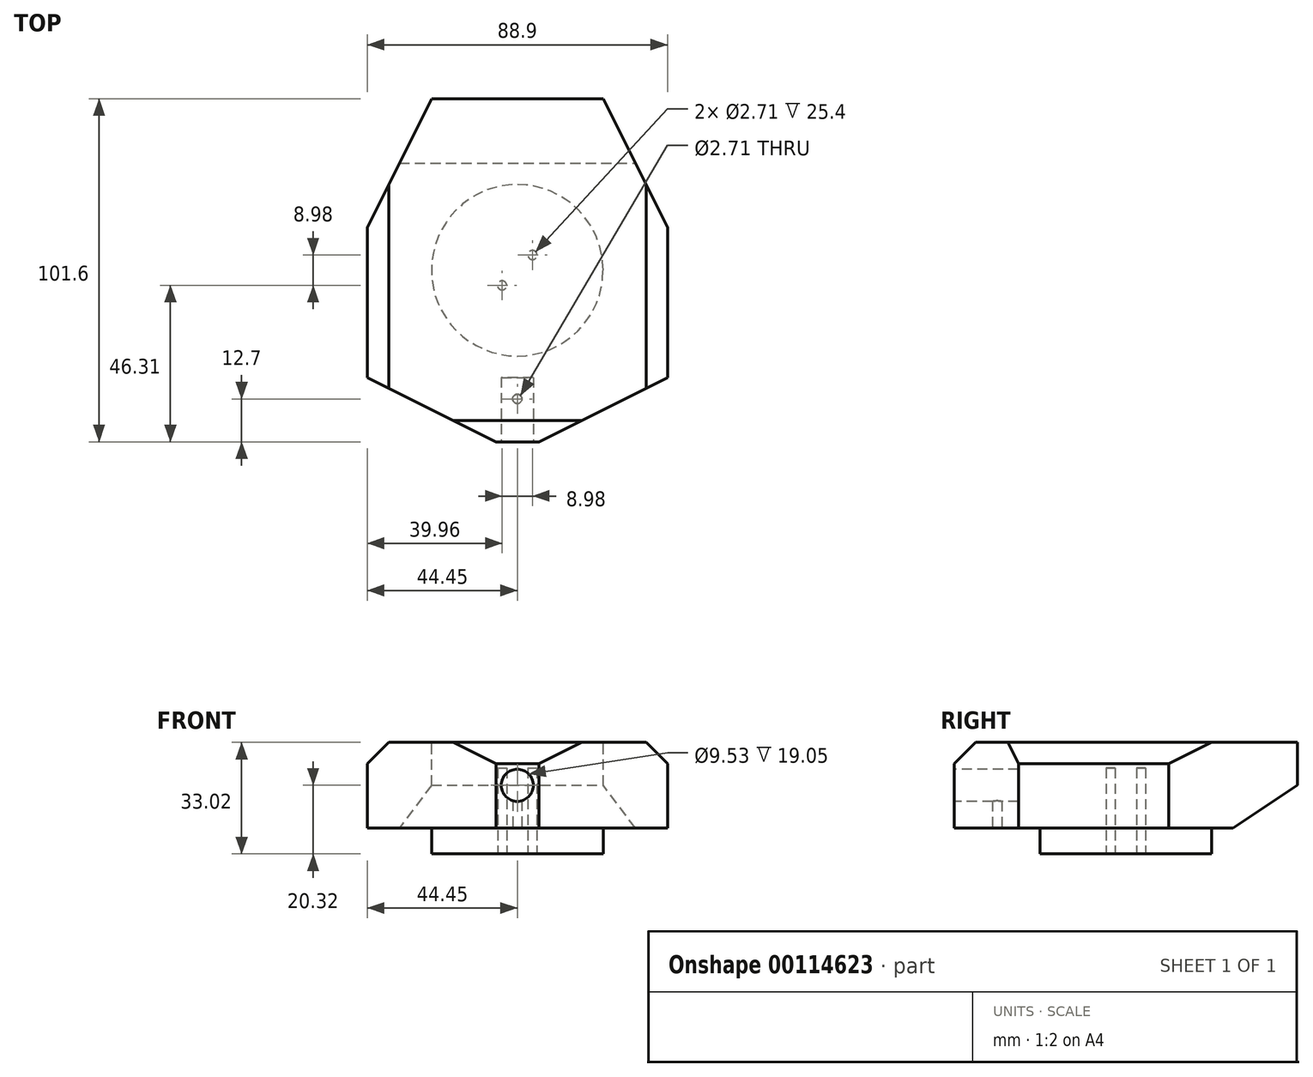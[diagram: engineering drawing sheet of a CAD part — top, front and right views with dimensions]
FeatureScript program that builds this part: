
annotation { "Feature Type Name" : "Feature", "Feature Type Description" : "" }
export const myFeature = defineFeature(function(context is Context, id is Id, definition is map)
    precondition{}
    {
        {
            var Q0;
            Q0=qCreatedBy(makeId("Front.planeOp"),FACE);
            var sketch = newSketch(context, id + "F0", { "sketchPlane" : qUnion([Q0])});
            skLineSegment(sketch, "E0.bottom", {"start": v(44.45, -12.7) * mm, "end": v(-44.45, -12.7) * mm});
            skLineSegment(sketch, "E0.top", {"start": v(44.45, 12.7) * mm, "end": v(-44.45, 12.7) * mm});
            skLineSegment(sketch, "E0.left", {"start": v(44.45, -12.7) * mm, "end": v(44.45, 12.7) * mm});
            skLineSegment(sketch, "E0.right", {"start": v(-44.45, -12.7) * mm, "end": v(-44.45, 12.7) * mm});
            skPoint(sketch, "E0.middle", {"position": v(0, 0) * mm});
            skSolve(sketch);
        }
        {
            var Q0;
            Q0 = qSketchRegion(id + "F0", true);
            extrude(context, id + "F1", {"entities" : qUnion([Q0]), "endBound" : BoundingType.SYMMETRIC, "depth" : 101.6 * mm});
        }
        {
            var Q0;
            Q0=makeQuery(id+"F1.opExtrude","SWEPT_FACE",FACE,{"disambiguationData":[OSD([sQuery(id+"F0.wireOp",EDGE,"E0.top")])]});
            var sketch = newSketch(context, id + "F2", { "sketchPlane" : qUnion([Q0])});
            skPoint(sketch, "E1", {"position": v(0, -50.8) * mm});
            skPoint(sketch, "E2", {"position": v(6.35, -50.8) * mm});
            skPoint(sketch, "E3", {"position": v(-6.35, -50.8) * mm});
            skPoint(sketch, "E4", {"position": v(-44.45, -50.8) * mm});
            skPoint(sketch, "E5", {"position": v(44.45, -50.8) * mm});
            skPoint(sketch, "E6", {"position": v(44.45, -31.75) * mm});
            skPoint(sketch, "E7", {"position": v(-44.45, -31.75) * mm});
            skLineSegment(sketch, "E8", {"start": v(-44.45, -31.75) * mm, "end": v(-6.35, -50.8) * mm});
            skLineSegment(sketch, "E9", {"start": v(-6.35, -50.8) * mm, "end": v(6.35, -50.8) * mm});
            skLineSegment(sketch, "E10", {"start": v(6.35, -50.8) * mm, "end": v(44.45, -31.75) * mm});
            skLineSegment(sketch, "E11", {"start": v(44.45, -31.75) * mm, "end": v(44.45, -50.8) * mm});
            skLineSegment(sketch, "E12", {"start": v(44.45, -50.8) * mm, "end": v(6.35, -50.8) * mm});
            skLineSegment(sketch, "E13", {"start": v(-6.35, -50.8) * mm, "end": v(-44.45, -50.8) * mm});
            skLineSegment(sketch, "E14", {"start": v(-44.45, -50.8) * mm, "end": v(-44.45, -31.75) * mm});
            skLineSegment(sketch, "E15", {"start": v(-44.45, 50.8) * mm, "end": v(-44.45, 12.7) * mm});
            skLineSegment(sketch, "E16", {"start": v(44.45, 50.8) * mm, "end": v(44.45, 12.7) * mm});
            skLineSegment(sketch, "E17", {"start": v(-44.45, 50.8) * mm, "end": v(-25.4, 50.8) * mm});
            skLineSegment(sketch, "E18", {"start": v(44.45, 50.8) * mm, "end": v(25.4, 50.8) * mm});
            skLineSegment(sketch, "E19", {"start": v(25.4, 50.8) * mm, "end": v(44.45, 12.7) * mm});
            skLineSegment(sketch, "E20", {"start": v(-25.4, 50.8) * mm, "end": v(-44.45, 12.7) * mm});
            skSolve(sketch);
        }
        {
            var Q0;
            Q0 = qSketchRegion(id + "F2", true);
            extrude(context, id + "F3", {"entities" : qUnion([Q0]), "operationType" : NewBodyOperationType.REMOVE, "oppositeDirection" : true, "depth" : 25.4 * mm});
        }
        {
            var Q0;
            Q0=qCreatedBy(makeId("Right.planeOp"),FACE);
            var sketch = newSketch(context, id + "F4", { "sketchPlane" : qUnion([Q0])});
            skLineSegment(sketch, "E21.0", {"start": v(50.8, -12.7) * mm, "end": v(50.8, 12.7) * mm, "construction": true});
            skPoint(sketch, "E22", {"position": v(50.8, 0) * mm});
            skLineSegment(sketch, "E23", {"start": v(50.8, 0) * mm, "end": v(50.8, -12.7) * mm, "construction": true});
            skLineSegment(sketch, "E24", {"start": v(50.8, -12.7) * mm, "end": v(31.75, -12.7) * mm, "construction": true});
            skLineSegment(sketch, "E25", {"start": v(31.75, -12.7) * mm, "end": v(50.8, 0) * mm});
            skLineSegment(sketch, "E26", {"start": v(31.75, -12.7) * mm, "end": v(50.8, -12.7) * mm});
            skLineSegment(sketch, "E27", {"start": v(50.8, 0) * mm, "end": v(50.8, -12.7) * mm});
            skSolve(sketch);
        }
        {
            var Q0;
            Q0 = qSketchRegion(id + "F4", true);
            extrude(context, id + "F5", {"entities" : qUnion([Q0]), "operationType" : NewBodyOperationType.REMOVE, "endBound" : BoundingType.THROUGH_ALL, "oppositeDirection" : true, "depth" : 25.4 * mm});
        }
        {
            var Q0;
            Q0=makeQuery(id+"F5.boolean.opBoolean","COPY",FACE,{"derivedFrom":makeQuery(id+"F5.opExtrude","CAP_FACE",FACE,{"disambiguationData":[OSD([sQuery(id+"F4.wireOp",EDGE,"E25"),sQuery(id+"F4.wireOp",EDGE,"E26"),sQuery(id+"F4.wireOp",EDGE,"E27")])],"isStart":true})});
            extrude(context, id + "F6", {"entities" : qUnion([Q0]), "operationType" : NewBodyOperationType.REMOVE, "endBound" : BoundingType.THROUGH_ALL, "oppositeDirection" : true, "depth" : 25.4 * mm});
        }
        {
            var Q0;
            Q0=makeQuery(id+"F3.boolean.opBoolean","COPY",EDGE,{"derivedFrom":makeQuery(id+"F3.opExtrude","CAP_EDGE",EDGE,{"disambiguationData":[OSD([sQuery(id+"F2.wireOp",EDGE,"E10")])],"isStart":true})});
            var Q1;
            Q1=makeQuery(id+"F1.opExtrude","CAP_EDGE",EDGE,{"disambiguationData":[OSD([sQuery(id+"F0.wireOp",EDGE,"E0.top")])],"isStart":false});
            var Q2;
            Q2=makeQuery(id+"F3.boolean.opBoolean","COPY",EDGE,{"derivedFrom":makeQuery(id+"F3.opExtrude","CAP_EDGE",EDGE,{"disambiguationData":[OSD([sQuery(id+"F2.wireOp",EDGE,"E8")])],"isStart":true})});
            var Q3;
            Q3=makeQuery(id+"F1.opExtrude","SWEPT_EDGE",EDGE,{"disambiguationData":[OSD([sQuery(id+"F0.wireOp",EDGE,"E0.top"),sQuery(id+"F0.wireOp",EDGE,"E0.right")])]});
            var Q4;
            Q4=makeQuery(id+"F3.boolean.opBoolean","COPY",EDGE,{"derivedFrom":makeQuery(id+"F3.opExtrude","CAP_EDGE",EDGE,{"disambiguationData":[OSD([sQuery(id+"F2.wireOp",EDGE,"E20")])],"isStart":true})});
            var Q5;
            Q5=makeQuery(id+"F1.opExtrude","SWEPT_EDGE",EDGE,{"disambiguationData":[OSD([sQuery(id+"F0.wireOp",EDGE,"E0.top"),sQuery(id+"F0.wireOp",EDGE,"E0.left")])]});
            var Q6;
            Q6=makeQuery(id+"F3.boolean.opBoolean","COPY",EDGE,{"derivedFrom":makeQuery(id+"F3.opExtrude","CAP_EDGE",EDGE,{"disambiguationData":[OSD([sQuery(id+"F2.wireOp",EDGE,"E19")])],"isStart":true})});
            chamfer(context, id + "F7", {"entities" : qUnion([Q0, Q1, Q2, Q3, Q4, Q5, Q6]), "width" : 6.35 * mm, "tangentPropagation" : true});
        }
        {
            var Q0;
            Q0=makeQuery(id+"F1.opExtrude","SWEPT_FACE",FACE,{"disambiguationData":[OSD([sQuery(id+"F0.wireOp",EDGE,"E0.bottom")])]});
            var sketch = newSketch(context, id + "F8", { "sketchPlane" : qUnion([Q0])});
            skCircle(sketch, "E28", {"center": v(0, 0) * mm, "radius": 25.4 * mm});
            skLineSegment(sketch, "E29", {"start": v(0, 0) * mm, "end": v(20.32, 0) * mm, "construction": true});
            skSolve(sketch);
        }
        {
            var Q0;
            Q0 = qSketchRegion(id + "F8", true);
            extrude(context, id + "F9", {"entities" : qUnion([Q0]), "operationType" : NewBodyOperationType.ADD, "depth" : 7.62 * mm});
        }
        {
            var Q0;
            Q0=makeQuery(id+"F9.opExtrude","CAP_FACE",FACE,{"disambiguationData":[OSD([sQuery(id+"F8.wireOp",EDGE,"E28")])],"isStart":false});
            var sketch = newSketch(context, id + "F10", { "sketchPlane" : qUnion([Q0])});
            skLineSegment(sketch, "E30", {"start": v(0, 0) * mm, "end": v(6.09, 0) * mm});
            skLineSegment(sketch, "E31", {"start": v(0, 0) * mm, "end": v(4.58, 4.58) * mm, "construction": true});
            skLineSegment(sketch, "E32", {"start": v(0, 0) * mm, "end": v(4.5, -4.5) * mm, "construction": true});
            skCircle(sketch, "E33", {"center": v(4.5, -4.5) * mm, "radius": 1.35 * mm});
            skCircle(sketch, "E34.MirrorC", {"center": v(-4.5, 4.5) * mm, "radius": 1.35 * mm});
            skSolve(sketch);
        }
        {
            var Q0;
            Q0 = qSketchRegion(id + "F10", true);
            extrude(context, id + "F11", {"entities" : qUnion([Q0]), "operationType" : NewBodyOperationType.REMOVE, "oppositeDirection" : true, "depth" : 25.4 * mm});
        }
        {
            var Q0;
            Q0=makeQuery(id+"F1.opExtrude","CAP_FACE",FACE,{"disambiguationData":[OSD([sQuery(id+"F0.wireOp",EDGE,"E0.bottom"),sQuery(id+"F0.wireOp",EDGE,"E0.top"),sQuery(id+"F0.wireOp",EDGE,"E0.left"),sQuery(id+"F0.wireOp",EDGE,"E0.right")])],"isStart":false});
            var sketch = newSketch(context, id + "F12", { "sketchPlane" : qUnion([Q0])});
            skCircle(sketch, "E35", {"center": v(0, 0) * mm, "radius": 4.76 * mm});
            skSolve(sketch);
        }
        {
            var Q0;
            Q0=makeQuery(id+"F12.imprint","IMPRINT",FACE,{"disambiguationData":[TD([[makeQuery(id+"F12.imprint","IMPRINT",EDGE,{"derivedFrom":sQuery(id+"F12.wireOp",EDGE,"E35")}),1.0]])]});
            extrude(context, id + "F13", {"entities" : qUnion([Q0]), "operationType" : NewBodyOperationType.REMOVE, "oppositeDirection" : true, "depth" : 19.05 * mm});
        }
        {
            var Q0;
            Q0=makeQuery(id+"F1.opExtrude","SWEPT_FACE",FACE,{"disambiguationData":[OSD([sQuery(id+"F0.wireOp",EDGE,"E0.bottom")])]});
            var sketch = newSketch(context, id + "F14", { "sketchPlane" : qUnion([Q0])});
            skLineSegment(sketch, "E36", {"start": v(0, 50.8) * mm, "end": v(0, 38.1) * mm, "construction": true});
            skPoint(sketch, "E36.endSnap0", {"position": v(0, 50.8) * mm});
            skCircle(sketch, "E37", {"center": v(0, 38.1) * mm, "radius": 1.35 * mm});
            skSolve(sketch);
        }
        {
            var Q0;
            Q0=makeQuery(id+"F14.imprint","IMPRINT",FACE,{"disambiguationData":[TD([[makeQuery(id+"F14.imprint","IMPRINT",EDGE,{"derivedFrom":sQuery(id+"F14.wireOp",EDGE,"E37")}),1.0]])]});
            extrude(context, id + "F15", {"entities" : qUnion([Q0]), "operationType" : NewBodyOperationType.REMOVE, "oppositeDirection" : true, "depth" : 12.7 * mm});
        }
    });
